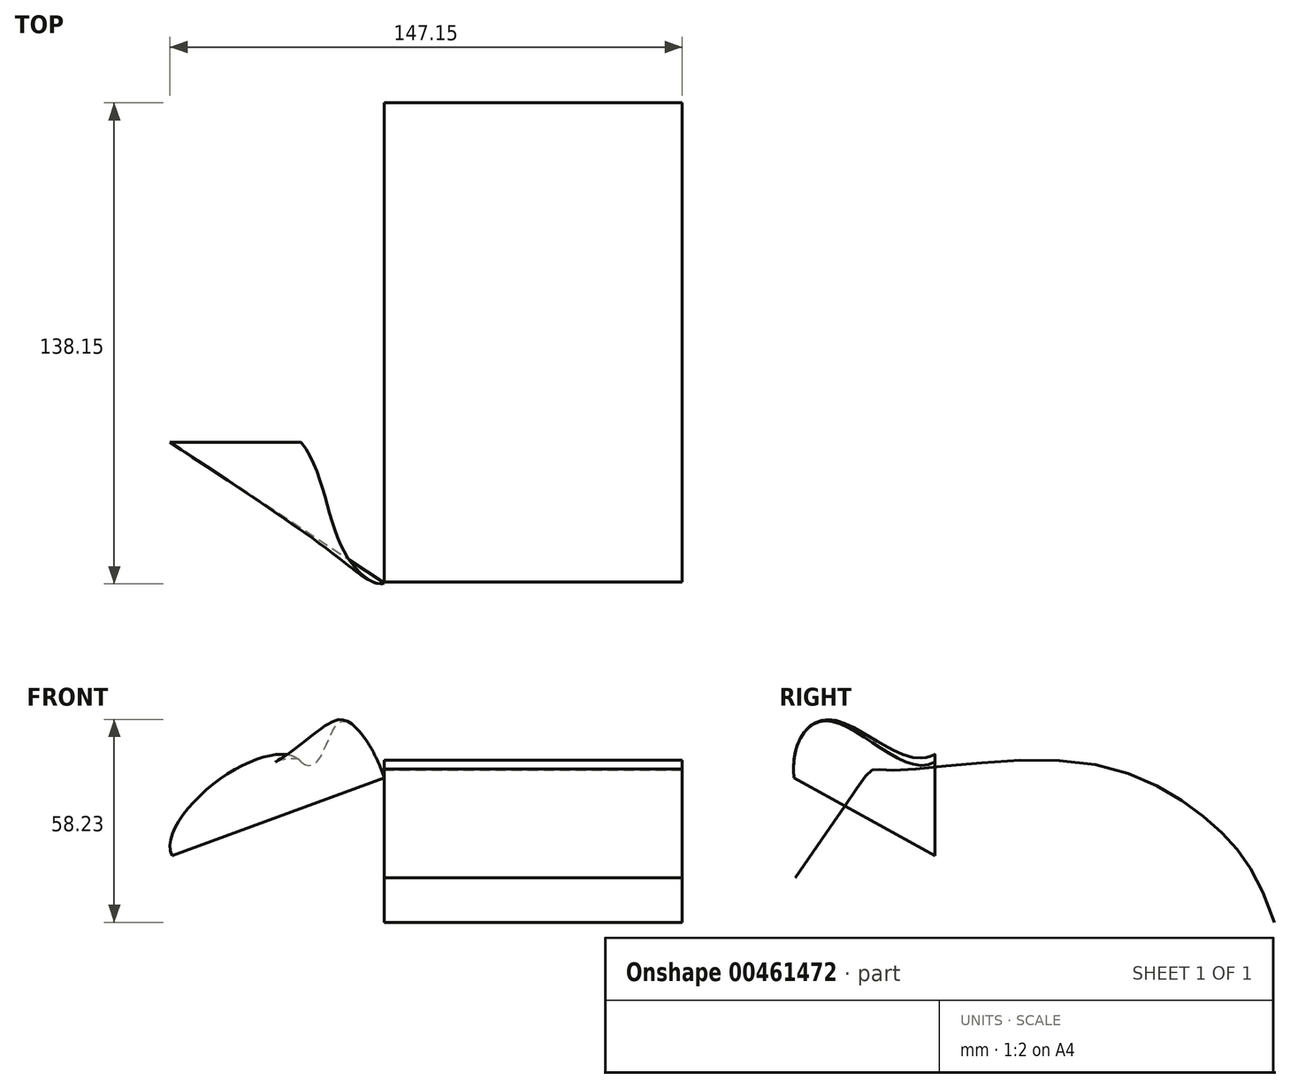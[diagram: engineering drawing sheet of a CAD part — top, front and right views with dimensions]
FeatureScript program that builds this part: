
annotation { "Feature Type Name" : "Feature", "Feature Type Description" : "" }
export const myFeature = defineFeature(function(context is Context, id is Id, definition is map)
    precondition{}
    {
        {
            var Q0;
            Q0=qCreatedBy(makeId("Right.planeOp"),FACE);
            var sketch = newSketch(context, id + "F0", { "sketchPlane" : qUnion([Q0])});
            skLineSegment(sketch, "E0", {"start": v(-40.08, 25.97) * mm, "end": v(-21.21, 53.23) * mm, "construction": true});
            skFitSpline(sketch, "E1", {"points": [v(-21.21, 53.23) * mm, v(-17.66, 57.02) * mm, v(-12.03, 56.81) * mm, v(42.97, 58.93) * mm], "startDerivative": vector(35.55, 51.36) * mm, "endDerivative": vector(126.12, -10.4) * mm, "construction": true});
            skFitSpline(sketch, "E2", {"points": [v(-40.08, 25.97) * mm, v(-21.21, 53.23) * mm, v(-17.66, 57.02) * mm, v(-12.03, 56.81) * mm, v(42.97, 58.93) * mm, v(80.72, 40.49) * mm, v(97.55, 13.15) * mm], "startDerivative": vector(117.34, 169.94) * mm, "endDerivative": vector(74.95, -224.85) * mm});
            skSolve(sketch);
        }
        {
            var Q0;
            Q0=sQuery(id+"F0.wireOp",EDGE,"E2");
            extrude(context, id + "F1", {"bodyType" : ToolBodyType.SURFACE, "surfaceEntities" : qUnion([Q0]), "depth" : 85.6 * mm});
        }
        {
            var Q0;
            Q0=qCreatedBy(makeId("Front.planeOp"),FACE);
            var sketch = newSketch(context, id + "F2", { "sketchPlane" : qUnion([Q0])});
            skFitSpline(sketch, "E3", {"points": [v(-61, 32.3) * mm, v(-42.91, 57.03) * mm, v(-23.88, 59.2) * mm], "startDerivative": vector(-16.8, 36.57) * mm, "endDerivative": vector(16.7, -25.25) * mm});
            skSolve(sketch);
        }
        {
            var Q0;
            Q0=qCreatedBy(makeId("Right.planeOp"),FACE);
            var sketch = newSketch(context, id + "F3", { "sketchPlane" : qUnion([Q0])});
            skPoint(sketch, "E4", {"position": v(-40.4, 54.66) * mm});
            skSolve(sketch);
        }
        {
            var Q0;
            Q0=qCreatedBy(makeId("Origin.pointOp"),VERTEX);
            var Q1;
            Q1=sQuery(id+"F3.wireOp",VERTEX,"E4");
            var Q2;
            Q2=sQuery(id+"F2.wireOp",VERTEX,"E3.end");
            cPlane(context, id + "F4", {"entities" : qUnion([Q0, Q1, Q2]), "cplaneType" : CPlaneType.THREE_POINT, "offset" : 25.4 * mm, "width" : 152.4 * mm, "height" : 152.4 * mm});
        }
        {
            var Q0;
            Q0=qCreatedBy(id+"F4.planeOp",FACE);
            var sketch = newSketch(context, id + "F5", { "sketchPlane" : qUnion([Q0])});
            skFitSpline(sketch, "E5", {"points": [v(0, 63.82) * mm, v(-33.49, 70.33) * mm, v(-45.29, 50.7) * mm], "startDerivative": vector(-49.49, -38.56) * mm, "endDerivative": vector(9.09, -62.58) * mm});
            skSolve(sketch);
        }
        {
            var Q0;
            Q0=sQuery(id+"F2.wireOp",EDGE,"E3");
            var Q1;
            Q1=sQuery(id+"F3.wireOp",VERTEX,"E4");
            var Q2;
            Q2=sQuery(id+"F5.wireOp",EDGE,"E5");
            loft(context, id + "F6", {"bodyType" : ToolBodyType.SURFACE, "addGuides" : true, "wireProfilesArray" : [{ "wireProfileEntities" : qUnion([Q0]) }, { "wireProfileEntities" : qUnion([Q1]) }], "guidesArray" : [{ "guideEntities" : qUnion([Q2]), "guideDerivativeType" : LoftGuideDerivativeType.DEFAULT, "guideDerivativeMagnitude" : 1 }]});
        }
    });
